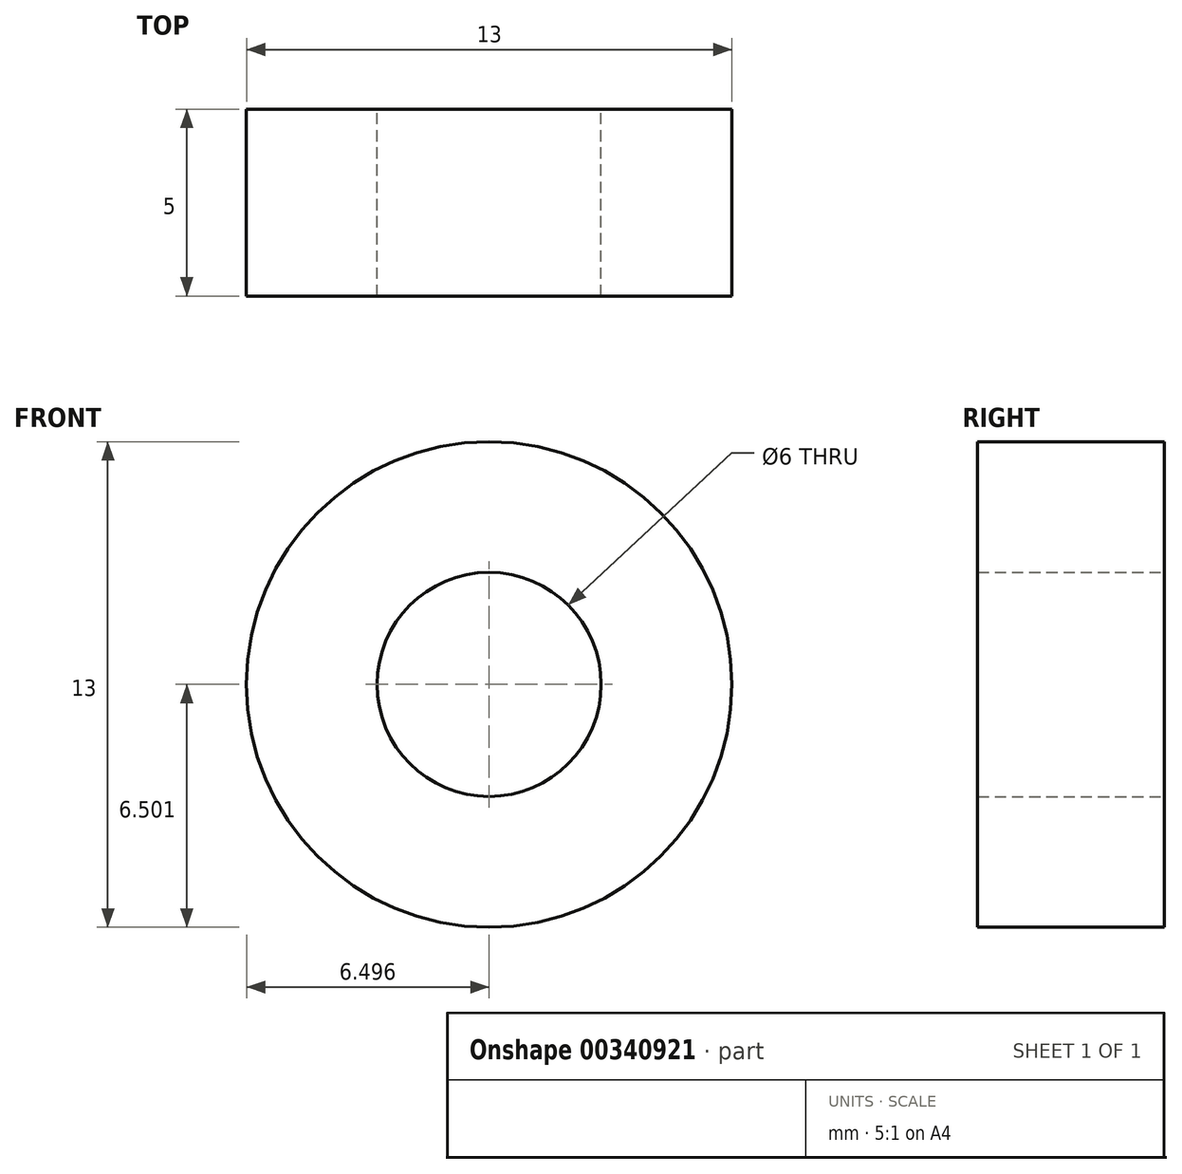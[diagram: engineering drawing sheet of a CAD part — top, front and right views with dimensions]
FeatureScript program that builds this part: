
annotation { "Feature Type Name" : "Feature", "Feature Type Description" : "" }
export const myFeature = defineFeature(function(context is Context, id is Id, definition is map)
    precondition{}
    {
        {
            var Q0;
            Q0=qCreatedBy(makeId("Front.planeOp"),FACE);
            var sketch = newSketch(context, id + "F0", { "sketchPlane" : qUnion([Q0])});
            skCircle(sketch, "E0", {"center": v(-28.7, 11.06) * mm, "radius": 3 * mm});
            skCircle(sketch, "E1", {"center": v(-28.7, 11.06) * mm, "radius": 6.5 * mm});
            skSolve(sketch);
        }
        {
            var Q0;
            Q0 = qSketchRegion(id + "F0", true);
            extrude(context, id + "F1", {"entities" : qUnion([Q0]), "depth" : 5 * mm, "offsetDistance" : 25 * mm});
        }
    });
